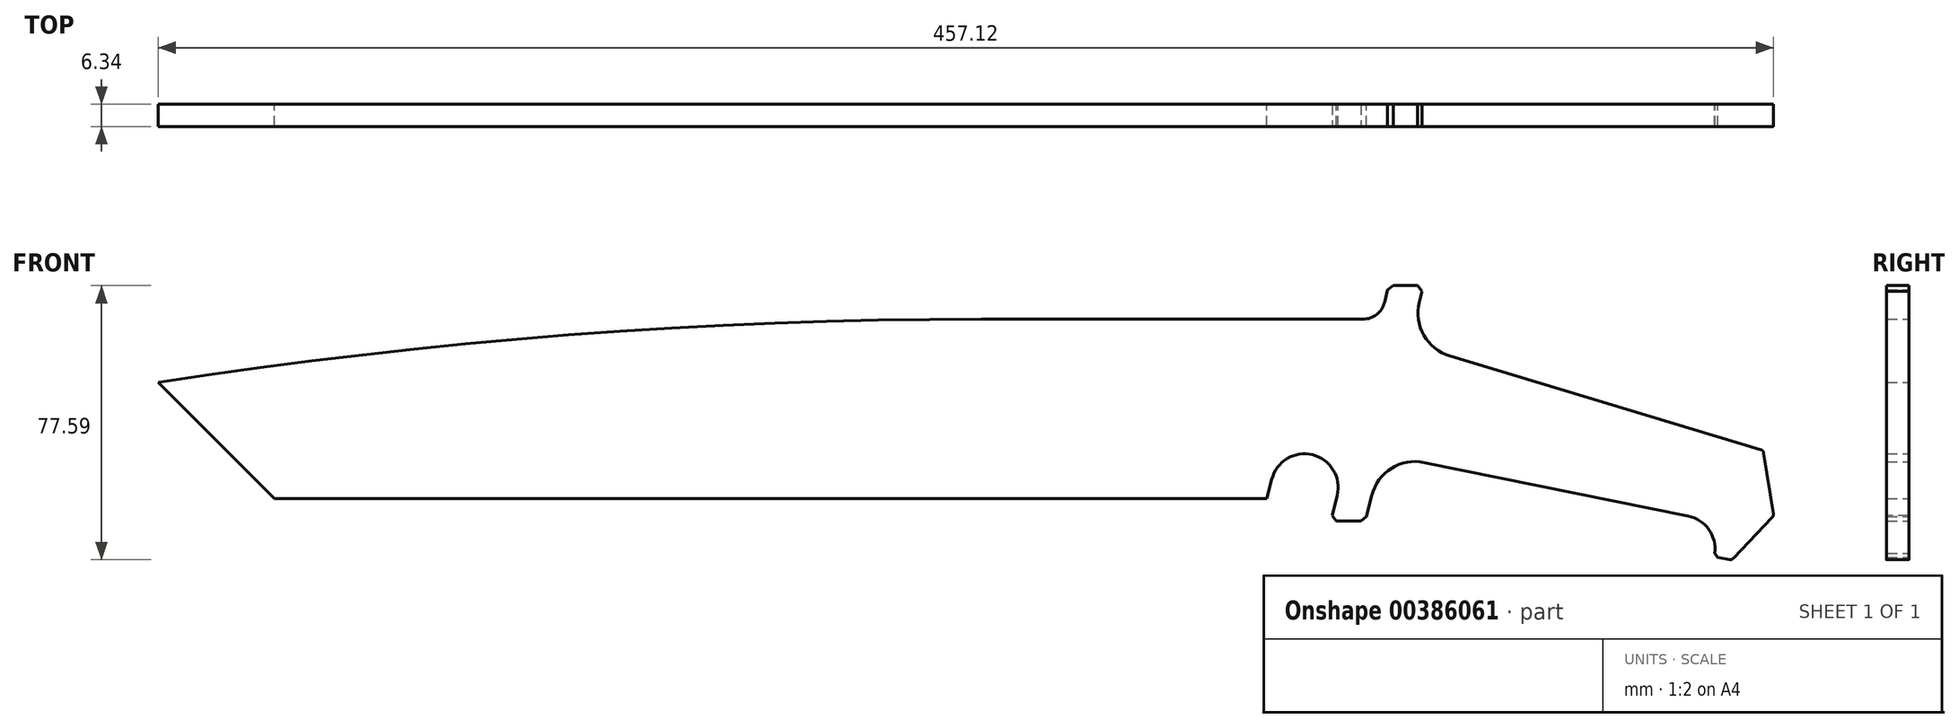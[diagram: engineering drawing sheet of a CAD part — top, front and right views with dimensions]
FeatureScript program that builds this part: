
annotation { "Feature Type Name" : "Feature", "Feature Type Description" : "" }
export const myFeature = defineFeature(function(context is Context, id is Id, definition is map)
    precondition{}
    {
        {
            var Q0;
            Q0=qCreatedBy(makeId("Front.planeOp"),FACE);
            var sketch = newSketch(context, id + "F0", { "sketchPlane" : qUnion([Q0])});
            skLineSegment(sketch, "E0", {"start": v(58.64, -18.88) * mm, "end": v(-222.29, -18.88) * mm});
            skLineSegment(sketch, "E1", {"start": v(-222.29, -18.88) * mm, "end": v(-255.17, 14.01) * mm});
            skLineSegment(sketch, "E2", {"start": v(-255.17, 14.01) * mm, "end": v(-22.19, 31.92) * mm});
            skLineSegment(sketch, "E3", {"start": v(-22.19, 31.92) * mm, "end": v(85.76, 31.92) * mm});
            skArc(sketch, "E4", {"start": v(85.76, 31.92) * mm, "mid": v(89.67, 33.27) * mm, "end": v(91.92, 36.74) * mm});
            skLineSegment(sketch, "E5", {"start": v(91.92, 36.74) * mm, "end": v(93.1, 41.45) * mm});
            skLineSegment(sketch, "E6", {"start": v(93.1, 41.45) * mm, "end": v(102.91, 41.45) * mm});
            skLineSegment(sketch, "E7", {"start": v(102.91, 41.45) * mm, "end": v(101.74, 36.74) * mm});
            skArc(sketch, "E8", {"start": v(101.74, 36.74) * mm, "mid": v(103.02, 27.39) * mm, "end": v(110.4, 21.5) * mm});
            skLineSegment(sketch, "E9", {"start": v(110.4, 21.5) * mm, "end": v(199.1, -5.19) * mm});
            skLineSegment(sketch, "E10", {"start": v(199.1, -5.19) * mm, "end": v(202.03, -23.74) * mm});
            skLineSegment(sketch, "E11", {"start": v(202.03, -23.74) * mm, "end": v(190.14, -36.26) * mm});
            skLineSegment(sketch, "E12", {"start": v(190.14, -36.26) * mm, "end": v(185.2, -35.25) * mm});
            skArc(sketch, "E13", {"start": v(185.2, -35.25) * mm, "mid": v(183.92, -27.98) * mm, "end": v(177.82, -23.82) * mm});
            skLineSegment(sketch, "E14", {"start": v(177.82, -23.82) * mm, "end": v(103.16, -8.63) * mm});
            skArc(sketch, "E15", {"start": v(103.16, -8.63) * mm, "mid": v(93.85, -10.34) * mm, "end": v(88.3, -18) * mm});
            skLineSegment(sketch, "E16", {"start": v(88.3, -18) * mm, "end": v(86.5, -25.23) * mm});
            skLineSegment(sketch, "E17", {"start": v(86.5, -25.23) * mm, "end": v(76.69, -25.23) * mm});
            skLineSegment(sketch, "E18", {"start": v(76.69, -25.23) * mm, "end": v(78.49, -18) * mm});
            skArc(sketch, "E19", {"start": v(78.49, -18) * mm, "mid": v(71.55, -6.46) * mm, "end": v(60, -13.4) * mm});
            skLineSegment(sketch, "E20", {"start": v(60, -13.4) * mm, "end": v(58.64, -18.88) * mm});
            skArc(sketch, "E21", {"start": v(-22.19, 31.92) * mm, "mid": v(-139.02, 27.44) * mm, "end": v(-255.17, 14.01) * mm});
            skLineSegment(sketch, "E22", {"start": v(-222.29, -18.88) * mm, "end": v(-217.03, -6.18) * mm});
            skLineSegment(sketch, "E23", {"start": v(-217.03, -6.18) * mm, "end": v(-238.5, 15.3) * mm});
            skLineSegment(sketch, "E24", {"start": v(69.25, -6.18) * mm, "end": v(-217.03, -6.18) * mm});
            skLineSegment(sketch, "E25", {"start": v(199.68, -8.89) * mm, "end": v(192.51, -33.76) * mm});
            skSolve(sketch);
        }
        {
            var Q0;
            Q0 = qSketchRegion(id + "F0", true);
            extrude(context, id + "F1", {"entities" : qUnion([Q0]), "depth" : 6.35 * mm, "symmetric" : true});
        }
        {
            var Q0;
            Q0=makeQuery(id+"F1.opExtrude","SWEPT_EDGE",EDGE,{"disambiguationData":[OSD([sQuery(id+"F0.wireOp",EDGE,"E5"),sQuery(id+"F0.wireOp",EDGE,"E6")])]});
            var Q1;
            Q1=makeQuery(id+"F1.opExtrude","SWEPT_EDGE",EDGE,{"disambiguationData":[OSD([sQuery(id+"F0.wireOp",EDGE,"E16"),sQuery(id+"F0.wireOp",EDGE,"E17")])]});
            chamfer(context, id + "F2", {"entities" : qUnion([Q0, Q1]), "chamferType" : ChamferType.TWO_OFFSETS, "width1" : 1.27 * mm, "oppositeDirection" : false, "width2" : 1.27 * mm, "tangentPropagation" : true});
        }
        {
            var Q0;
            Q0=makeQuery(id+"F1.opExtrude","SWEPT_EDGE",EDGE,{"disambiguationData":[OSD([sQuery(id+"F0.wireOp",EDGE,"E6"),sQuery(id+"F0.wireOp",EDGE,"E7")])]});
            var Q1;
            Q1=makeQuery(id+"F1.opExtrude","SWEPT_EDGE",EDGE,{"disambiguationData":[OSD([sQuery(id+"F0.wireOp",EDGE,"E17"),sQuery(id+"F0.wireOp",EDGE,"E18")])]});
            chamfer(context, id + "F3", {"entities" : qUnion([Q0, Q1]), "width" : 1.27 * mm, "tangentPropagation" : true});
        }
        {
            var Q0;
            Q0=makeQuery(id+"F1.opExtrude","SWEPT_EDGE",EDGE,{"disambiguationData":[OSD([sQuery(id+"F0.wireOp",EDGE,"E12"),sQuery(id+"F0.wireOp",EDGE,"E13")])]});
            chamfer(context, id + "F4", {"entities" : qUnion([Q0]), "width" : 1.02 * mm, "tangentPropagation" : true});
        }
        {
            var Q0;
            Q0=makeQuery(id+"F1.opExtrude","SWEPT_EDGE",EDGE,{"disambiguationData":[OSD([sQuery(id+"F0.wireOp",EDGE,"E10"),sQuery(id+"F0.wireOp",EDGE,"E11")])]});
            var Q1;
            Q1=makeQuery(id+"F1.opExtrude","SWEPT_EDGE",EDGE,{"disambiguationData":[OSD([sQuery(id+"F0.wireOp",EDGE,"E9"),sQuery(id+"F0.wireOp",EDGE,"E10")])]});
            var Q2;
            Q2=makeQuery(id+"F1.opExtrude","SWEPT_EDGE",EDGE,{"disambiguationData":[OSD([sQuery(id+"F0.wireOp",EDGE,"E11"),sQuery(id+"F0.wireOp",EDGE,"E12")])]});
            fillet(context, id + "F5", {"entities" : qUnion([Q0, Q1, Q2]), "radius" : 1.27 * mm, "tangentPropagation" : true, "allowEdgeOverflow" : false});
        }
    });
